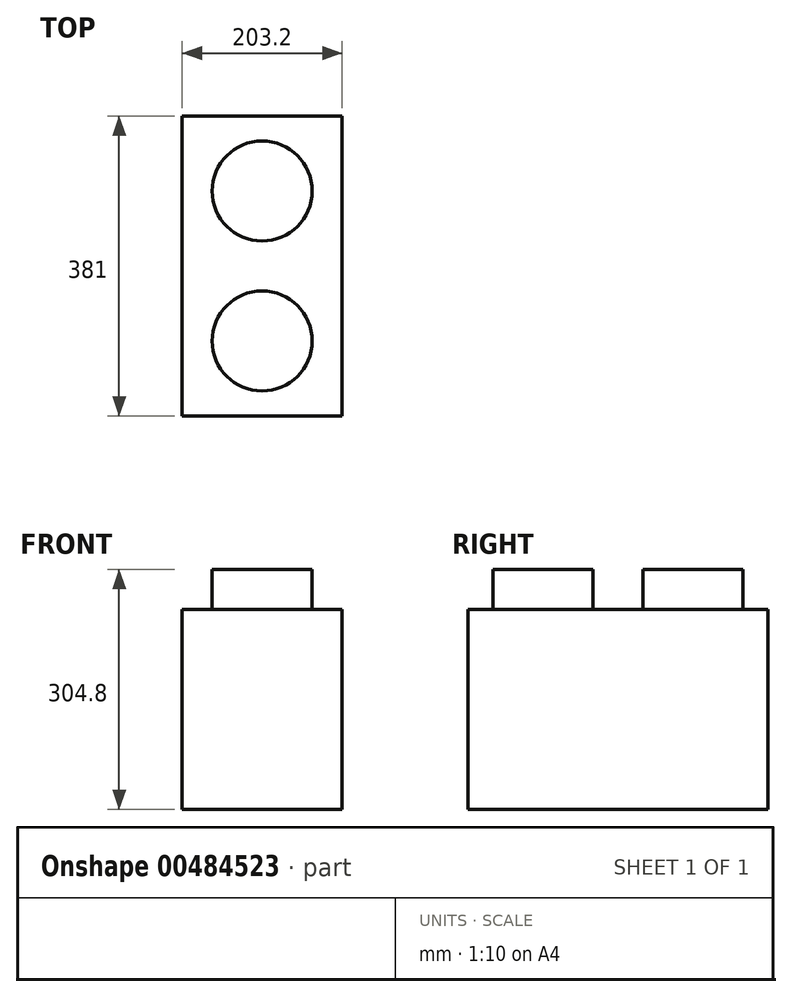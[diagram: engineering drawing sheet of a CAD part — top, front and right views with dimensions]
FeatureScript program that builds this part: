
annotation { "Feature Type Name" : "Feature", "Feature Type Description" : "" }
export const myFeature = defineFeature(function(context is Context, id is Id, definition is map)
    precondition{}
    {
        {
            var Q0;
            Q0=qCreatedBy(makeId("Right.planeOp"),FACE);
            var sketch = newSketch(context, id + "F0", { "sketchPlane" : qUnion([Q0])});
            skLineSegment(sketch, "E0.bottom", {"start": v(-400.73, -160.06) * mm, "end": v(-19.73, -160.06) * mm});
            skLineSegment(sketch, "E0.top", {"start": v(-400.73, -414.06) * mm, "end": v(-19.73, -414.06) * mm});
            skLineSegment(sketch, "E0.left", {"start": v(-400.73, -160.06) * mm, "end": v(-400.73, -414.06) * mm});
            skLineSegment(sketch, "E0.right", {"start": v(-19.73, -160.06) * mm, "end": v(-19.73, -414.06) * mm});
            skSolve(sketch);
        }
        {
            var Q0;
            Q0=makeQuery(id+"F0.imprint","IMPRINT",FACE,{"disambiguationData":[TD([[makeQuery(id+"F0.imprint","IMPRINT",EDGE,{"derivedFrom":sQuery(id+"F0.wireOp",EDGE,"E0.bottom")}),-1.0]])]});
            extrude(context, id + "F1", {"entities" : qUnion([Q0]), "depth" : 203.2 * mm});
        }
        {
            var Q0;
            Q0=makeQuery(id+"F1.opExtrude","SWEPT_FACE",FACE,{"disambiguationData":[OSD([sQuery(id+"F0.wireOp",EDGE,"E0.bottom")])]});
            var sketch = newSketch(context, id + "F2", { "sketchPlane" : qUnion([Q0])});
            skPoint(sketch, "E1.startSnap0", {"position": v(101.6, -19.73) * mm});
            skCircle(sketch, "E2", {"center": v(101.6, -114.98) * mm, "radius": 63.5 * mm});
            skSolve(sketch);
        }
        {
            var Q0;
            Q0=makeQuery(id+"F2.imprint","IMPRINT",FACE,{"disambiguationData":[TD([[makeQuery(id+"F2.imprint","IMPRINT",EDGE,{"derivedFrom":sQuery(id+"F2.wireOp",EDGE,"E2")}),1.0]])]});
            extrude(context, id + "F3", {"entities" : qUnion([Q0]), "depth" : 50.8 * mm});
        }
        {
            var Q0;
            Q0=makeQuery(id+"F1.opExtrude","SWEPT_FACE",FACE,{"disambiguationData":[OSD([sQuery(id+"F0.wireOp",EDGE,"E0.bottom")])]});
            var sketch = newSketch(context, id + "F4", { "sketchPlane" : qUnion([Q0])});
            skCircle(sketch, "E3", {"center": v(101.6, -305.48) * mm, "radius": 63.5 * mm});
            skSolve(sketch);
        }
        {
            var Q0;
            Q0=makeQuery(id+"F4.imprint","IMPRINT",FACE,{"disambiguationData":[TD([[makeQuery(id+"F4.imprint","IMPRINT",EDGE,{"derivedFrom":sQuery(id+"F4.wireOp",EDGE,"E3")}),1.0]])]});
            extrude(context, id + "F5", {"entities" : qUnion([Q0]), "operationType" : NewBodyOperationType.ADD, "depth" : 50.8 * mm});
        }
        {
            var Q0;
            Q0=makeQuery(id+"F1.opExtrude","SWEPT_FACE",FACE,{"disambiguationData":[OSD([sQuery(id+"F0.wireOp",EDGE,"E0.top")])]});
            var sketch = newSketch(context, id + "F6", { "sketchPlane" : qUnion([Q0])});
            skCircle(sketch, "E4", {"center": v(101.6, 210.23) * mm, "radius": 38.1 * mm});
            skCircle(sketch, "E5", {"center": v(101.6, 210.23) * mm, "radius": 12.7 * mm});
            skLineSegment(sketch, "E6.bottom", {"start": v(177.8, 388.03) * mm, "end": v(25.4, 388.03) * mm});
            skLineSegment(sketch, "E6.top", {"start": v(177.8, 32.43) * mm, "end": v(25.4, 32.43) * mm});
            skLineSegment(sketch, "E6.left", {"start": v(177.8, 388.03) * mm, "end": v(177.8, 32.43) * mm});
            skLineSegment(sketch, "E6.right", {"start": v(25.4, 388.03) * mm, "end": v(25.4, 32.43) * mm});
            skSolve(sketch);
        }
        {
            var Q0;
            Q0=makeQuery(id+"F6.imprint","IMPRINT",FACE,{"disambiguationData":[TD([[makeQuery(id+"F6.imprint","IMPRINT",EDGE,{"derivedFrom":sQuery(id+"F6.wireOp",EDGE,"E5")}),1.0]])]});
            extrude(context, id + "F7", {"entities" : qUnion([Q0]), "operationType" : NewBodyOperationType.ADD, "oppositeDirection" : true, "depth" : 152.4 * mm});
        }
    });
